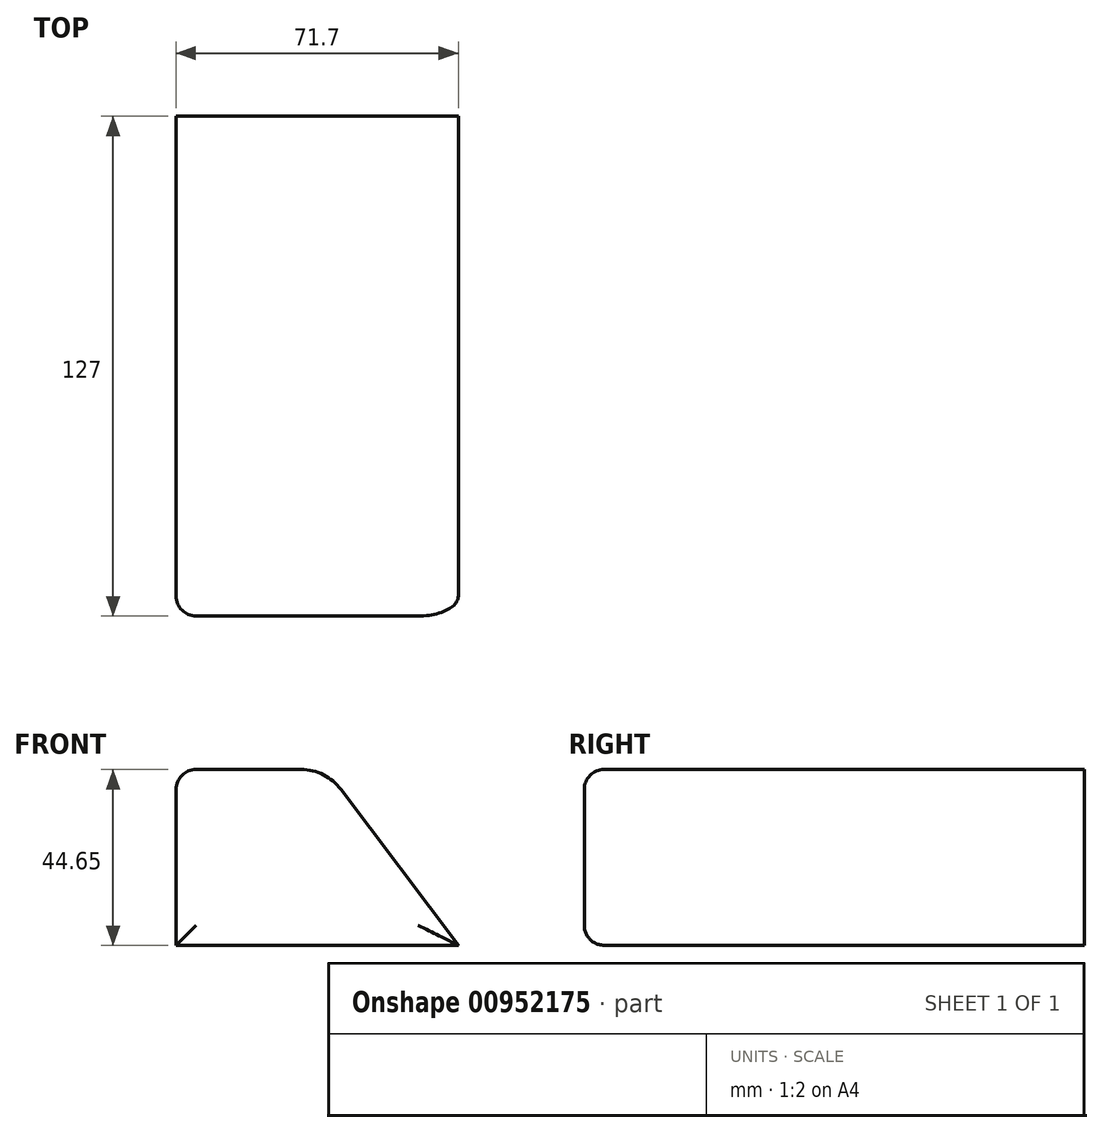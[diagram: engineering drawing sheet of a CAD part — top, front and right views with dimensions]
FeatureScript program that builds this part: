
annotation { "Feature Type Name" : "Feature", "Feature Type Description" : "" }
export const myFeature = defineFeature(function(context is Context, id is Id, definition is map)
    precondition{}
    {
        {
            var Q0;
            Q0=qCreatedBy(makeId("Front.planeOp"),FACE);
            var sketch = newSketch(context, id + "F0", { "sketchPlane" : qUnion([Q0])});
            skLineSegment(sketch, "E0", {"start": v(-41.96, 0) * mm, "end": v(-41.96, 44.65) * mm});
            skLineSegment(sketch, "E1", {"start": v(-41.96, 44.65) * mm, "end": v(-3.86, 44.65) * mm});
            skLineSegment(sketch, "E2", {"start": v(-3.86, 44.65) * mm, "end": v(29.74, 0) * mm});
            skLineSegment(sketch, "E3", {"start": v(29.74, 0) * mm, "end": v(-41.96, 0) * mm});
            skSolve(sketch);
        }
        {
            var Q0;
            Q0=makeQuery(id+"F0.imprint","IMPRINT",FACE,{"disambiguationData":[TD([[makeQuery(id+"F0.imprint","IMPRINT",EDGE,{"derivedFrom":sQuery(id+"F0.wireOp",EDGE,"E0")}),-1.0]])]});
            extrude(context, id + "F1", {"entities" : qUnion([Q0]), "depth" : 127 * mm, "offsetDistance" : 25.4 * mm});
        }
        {
            var Q0;
            Q0=makeQuery(id+"F1.opExtrude","SWEPT_EDGE",EDGE,{"disambiguationData":[OSD([sQuery(id+"F0.wireOp",EDGE,"E1"),sQuery(id+"F0.wireOp",EDGE,"E2")])]});
            fillet(context, id + "F2", {"entities" : qUnion([Q0]), "radius" : 12.7 * mm, "tangentPropagation" : true, "allowEdgeOverflow" : false});
        }
        {
            var Q0;
            Q0=makeQuery(id+"F1.opExtrude","CAP_FACE",FACE,{"disambiguationData":[OSD([sQuery(id+"F0.wireOp",EDGE,"E0"),sQuery(id+"F0.wireOp",EDGE,"E1"),sQuery(id+"F0.wireOp",EDGE,"E2"),sQuery(id+"F0.wireOp",EDGE,"E3")])],"isStart":false});
            var Q1;
            Q1=makeQuery(id+"F1.opExtrude","SWEPT_EDGE",EDGE,{"disambiguationData":[OSD([sQuery(id+"F0.wireOp",EDGE,"E0"),sQuery(id+"F0.wireOp",EDGE,"E1")])]});
            fillet(context, id + "F3", {"entities" : qUnion([Q0, Q1]), "radius" : 5.08 * mm, "tangentPropagation" : true, "allowEdgeOverflow" : false});
        }
    });
